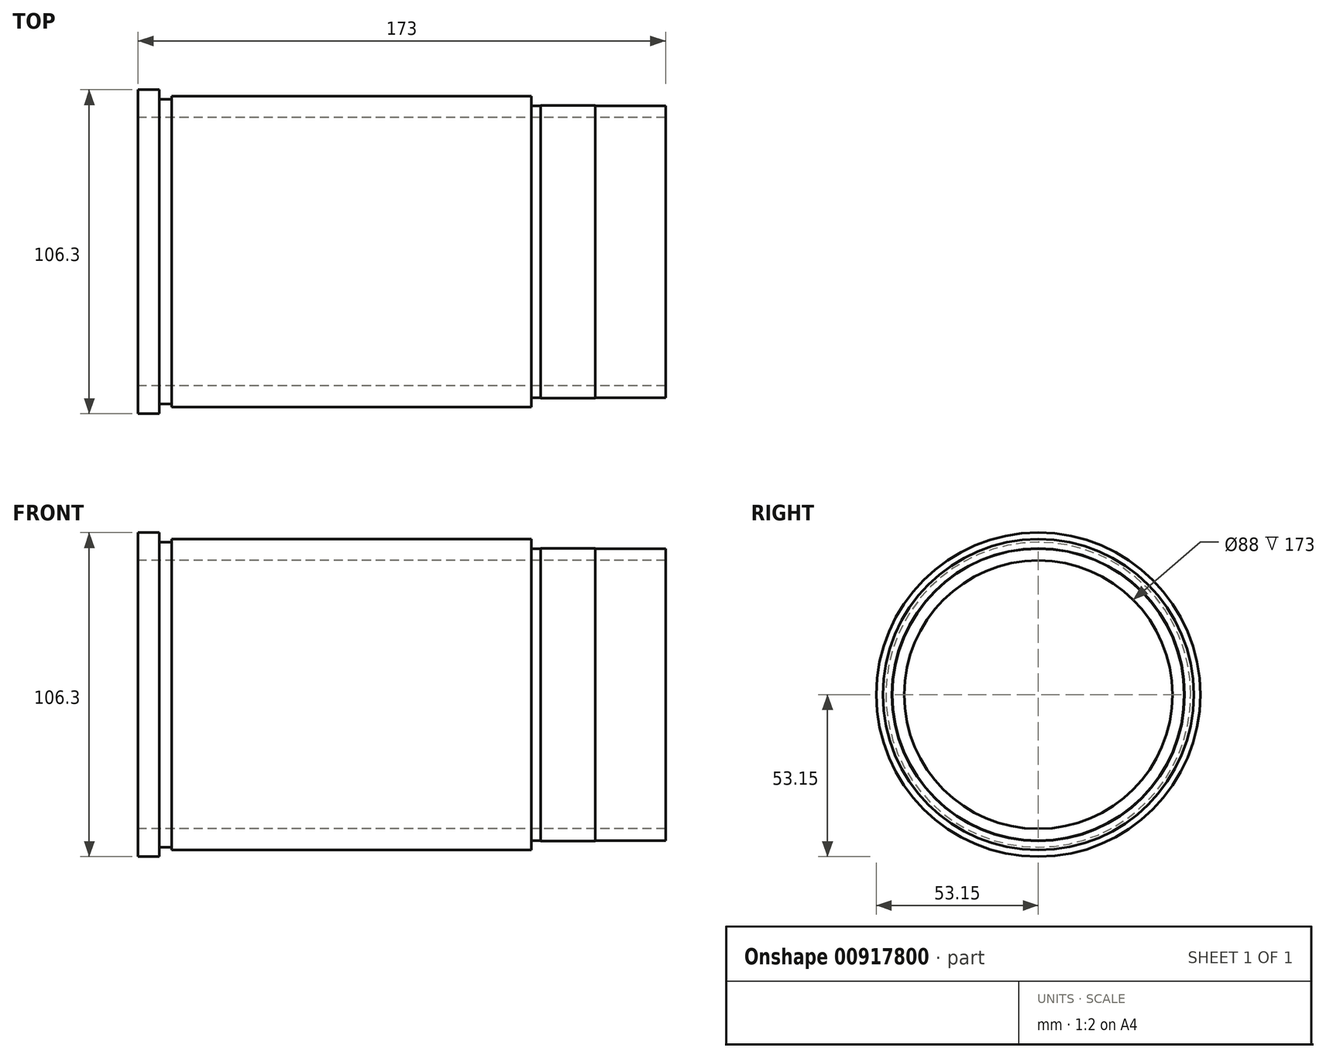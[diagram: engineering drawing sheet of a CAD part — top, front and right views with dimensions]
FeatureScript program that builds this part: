
annotation { "Feature Type Name" : "Feature", "Feature Type Description" : "" }
export const myFeature = defineFeature(function(context is Context, id is Id, definition is map)
    precondition{}
    {
        {
            var Q0;
            Q0=qCreatedBy(makeId("Front.planeOp"),FACE);
            var sketch = newSketch(context, id + "F0", { "sketchPlane" : qUnion([Q0])});
            skLineSegment(sketch, "E0", {"start": v(-235.12, 0) * mm, "end": v(157.74, 0) * mm, "construction": true});
            skLineSegment(sketch, "E1", {"start": v(-142.5, 44) * mm, "end": v(-142.5, 53.15) * mm});
            skLineSegment(sketch, "E2", {"start": v(-142.5, 53.15) * mm, "end": v(-135.5, 53.15) * mm});
            skLineSegment(sketch, "E3", {"start": v(-135.5, 53.15) * mm, "end": v(-135.5, 50) * mm});
            skLineSegment(sketch, "E4", {"start": v(-10.5, 48) * mm, "end": v(7.5, 48) * mm});
            skLineSegment(sketch, "E5", {"start": v(30.5, 47.9) * mm, "end": v(30.5, 44) * mm});
            skLineSegment(sketch, "E6", {"start": v(30.5, 44) * mm, "end": v(-142.5, 44) * mm});
            skLineSegment(sketch, "E7", {"start": v(-13.5, 48) * mm, "end": v(-13.5, 51) * mm});
            skLineSegment(sketch, "E8", {"start": v(-13.5, 51) * mm, "end": v(-131.5, 51) * mm});
            skLineSegment(sketch, "E9", {"start": v(-131.5, 51) * mm, "end": v(-131.5, 50) * mm});
            skLineSegment(sketch, "E10", {"start": v(-131.5, 50) * mm, "end": v(-135.5, 50) * mm});
            skLineSegment(sketch, "E11.MirrorCS", {"start": v(-131.5, -51) * mm, "end": v(-131.5, -50) * mm});
            skLineSegment(sketch, "E12.MirrorCS", {"start": v(30.5, -48) * mm, "end": v(30.5, -44) * mm});
            skLineSegment(sketch, "E13.MirrorCS", {"start": v(-131.5, -50) * mm, "end": v(-135.5, -50) * mm});
            skLineSegment(sketch, "E14.MirrorCS", {"start": v(-135.5, -53.15) * mm, "end": v(-135.5, -50) * mm});
            skLineSegment(sketch, "E15.MirrorCS", {"start": v(-13.5, -51) * mm, "end": v(-131.5, -51) * mm});
            skLineSegment(sketch, "E16.MirrorCS", {"start": v(-13.5, -48) * mm, "end": v(-13.5, -51) * mm});
            skLineSegment(sketch, "E17.MirrorCS", {"start": v(-13.5, -48) * mm, "end": v(30.5, -48) * mm});
            skLineSegment(sketch, "E18.MirrorCS", {"start": v(-142.5, -44) * mm, "end": v(-142.5, -53.15) * mm});
            skLineSegment(sketch, "E19.MirrorCS", {"start": v(-142.5, -53.15) * mm, "end": v(-135.5, -53.15) * mm});
            skLineSegment(sketch, "E20.MirrorCS", {"start": v(30.5, -44) * mm, "end": v(-142.5, -44) * mm});
            skLineSegment(sketch, "E21", {"start": v(-10.5, 48) * mm, "end": v(-10.5, 47.9) * mm});
            skLineSegment(sketch, "E22", {"start": v(-10.5, 47.9) * mm, "end": v(-13.5, 47.9) * mm});
            skLineSegment(sketch, "E23", {"start": v(-13.5, 47.9) * mm, "end": v(-13.5, 48) * mm});
            skLineSegment(sketch, "E24", {"start": v(7.5, 48) * mm, "end": v(7.5, 47.9) * mm});
            skLineSegment(sketch, "E25", {"start": v(7.5, 47.9) * mm, "end": v(30.5, 47.9) * mm});
            skSolve(sketch);
        }
        {
            var Q0;
            Q0=makeQuery(id+"F0.imprint","IMPRINT",FACE,{"disambiguationData":[TD([[makeQuery(id+"F0.imprint","IMPRINT",EDGE,{"derivedFrom":sQuery(id+"F0.wireOp",EDGE,"E1")}),-1.0]])]});
            var Q1;
            Q1=sQuery(id+"F0.wireOp",EDGE,"E0");
            revolve(context, id + "F1", {"surfaceOperationType" : NewSurfaceOperationType.NEW, "entities" : qUnion([Q0]), "axis" : qUnion([Q1]), "revolveType" : RevolveType.FULL});
        }
    });
